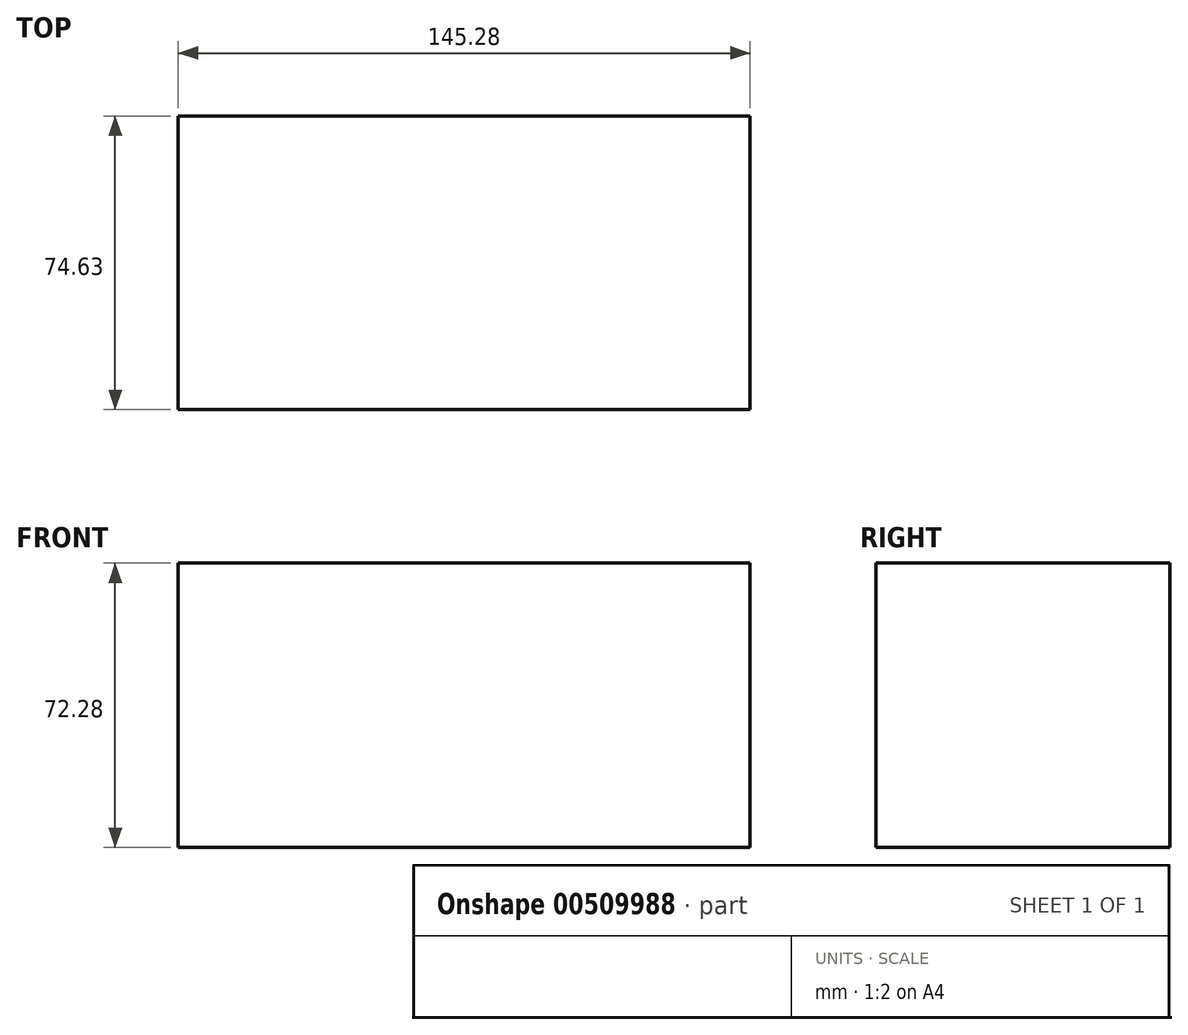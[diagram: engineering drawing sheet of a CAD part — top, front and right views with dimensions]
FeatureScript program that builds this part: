
annotation { "Feature Type Name" : "Feature", "Feature Type Description" : "" }
export const myFeature = defineFeature(function(context is Context, id is Id, definition is map)
    precondition{}
    {
        {
            var Q0;
            Q0=qCreatedBy(makeId("Front.planeOp"),FACE);
            var sketch = newSketch(context, id + "F0", { "sketchPlane" : qUnion([Q0])});
            skLineSegment(sketch, "E0.bottom", {"start": v(-72.5, 61.82) * mm, "end": v(75.52, 61.82) * mm});
            skLineSegment(sketch, "E0.top", {"start": v(-72.5, -11.8) * mm, "end": v(75.52, -11.8) * mm});
            skLineSegment(sketch, "E0.left", {"start": v(-72.5, 61.82) * mm, "end": v(-72.5, -11.8) * mm});
            skLineSegment(sketch, "E0.right", {"start": v(75.52, 61.82) * mm, "end": v(75.52, -11.8) * mm});
            skSolve(sketch);
        }
        {
            var Q0;
            Q0=qCreatedBy(makeId("Right.planeOp"),FACE);
            var sketch = newSketch(context, id + "F1", { "sketchPlane" : qUnion([Q0])});
            skLineSegment(sketch, "E1.bottom", {"start": v(0, 59.43) * mm, "end": v(74.63, 59.43) * mm});
            skLineSegment(sketch, "E1.top", {"start": v(0, -12.85) * mm, "end": v(74.63, -12.85) * mm});
            skLineSegment(sketch, "E1.left", {"start": v(0, 59.43) * mm, "end": v(0, -12.85) * mm});
            skLineSegment(sketch, "E1.right", {"start": v(74.63, 59.43) * mm, "end": v(74.63, -12.85) * mm});
            skSolve(sketch);
        }
        {
            var Q0;
            Q0=makeQuery(id+"F1.imprint","IMPRINT",FACE,{"disambiguationData":[TD([[makeQuery(id+"F1.imprint","IMPRINT",EDGE,{"derivedFrom":sQuery(id+"F1.wireOp",EDGE,"E1.bottom")}),-1.0]])]});
            var sketch = newSketch(context, id + "F2", { "sketchPlane" : qUnion([Q0])});
            skLineSegment(sketch, "E2.0.0", {"start": v(0, 61.82) * mm, "end": v(0, -11.8) * mm});
            skLineSegment(sketch, "E2.0.2", {"start": v(0, -11.8) * mm, "end": v(0, 61.82) * mm});
            skSolve(sketch);
        }
        {
            var Q0;
            Q0 = qSketchRegion(id + "F1", true);
            var Q1;
            {var subQ1=makeQuery(id+"F1.imprint","IMPRINT",EDGE,{"derivedFrom":sQuery(id+"F1.wireOp",EDGE,"E1.bottom")});Q1=makeQuery(id+"F2.imprint","IMPRINT",FACE,{"disambiguationData":[TD([[makeQuery(id+"F2.imprint","IMPRINT",EDGE,{"derivedFrom":subQ1}),-1.0]])]});}
            extrude(context, id + "F3", {"entities" : qUnion([Q0, Q1]), "oppositeDirection" : true, "depth" : 72.4 * mm, "hasSecondDirection" : true, "secondDirectionOppositeDirection" : false, "secondDirectionDepth" : 72.87 * mm});
        }
    });
